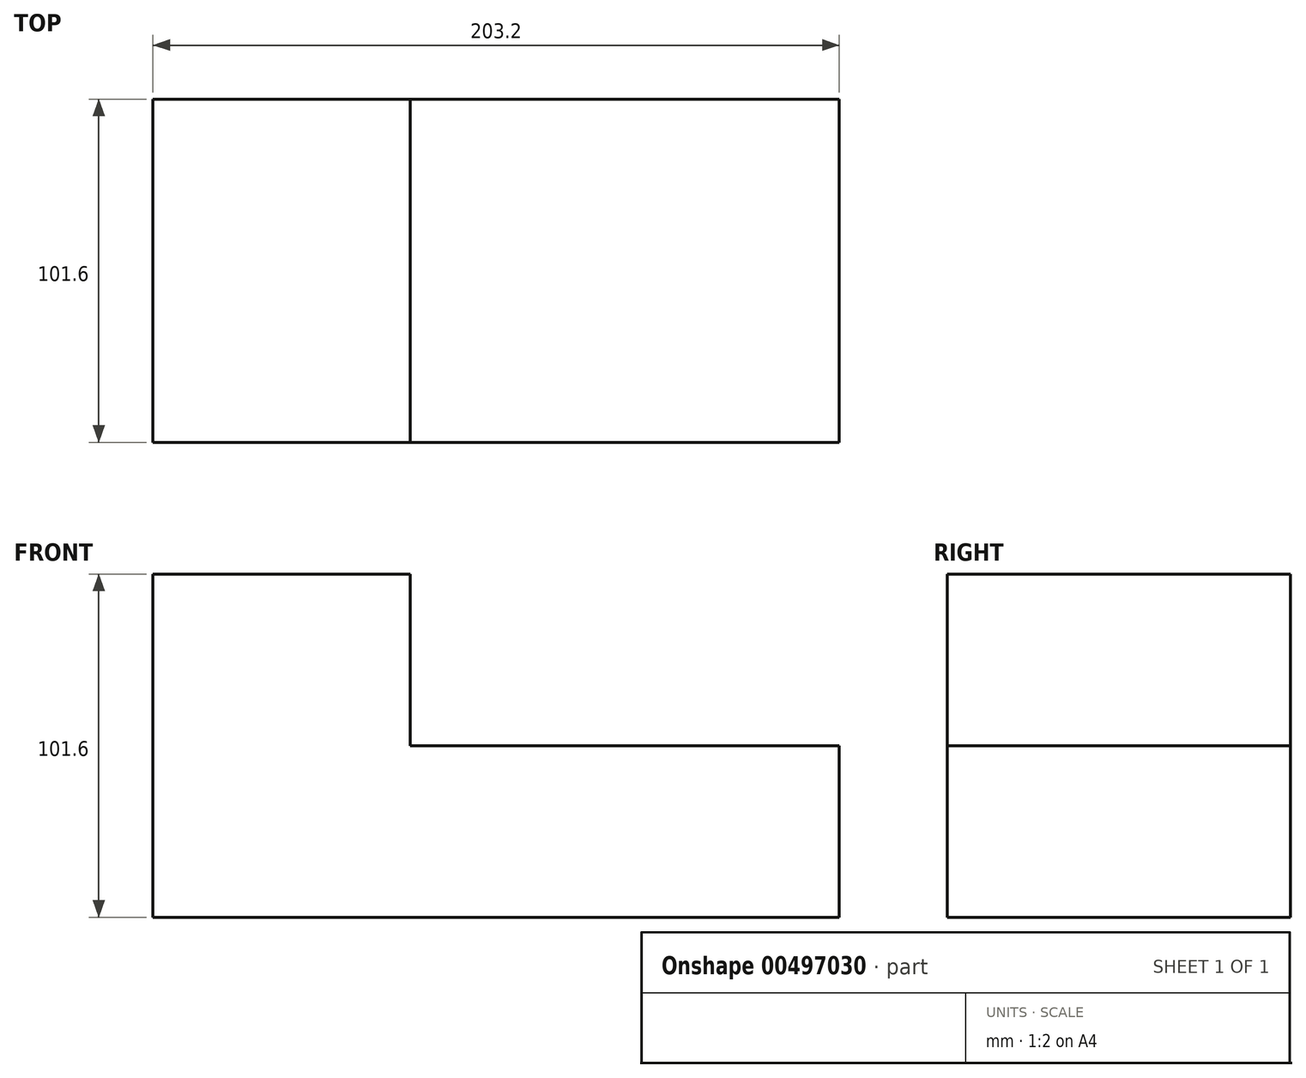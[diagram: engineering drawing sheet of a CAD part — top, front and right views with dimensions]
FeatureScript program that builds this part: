
annotation { "Feature Type Name" : "Feature", "Feature Type Description" : "" }
export const myFeature = defineFeature(function(context is Context, id is Id, definition is map)
    precondition{}
    {
        {
            var Q0;
            Q0=qCreatedBy(makeId("Front.planeOp"),FACE);
            var sketch = newSketch(context, id + "F0", { "sketchPlane" : qUnion([Q0])});
            skLineSegment(sketch, "E0.bottom", {"start": v(0, 0) * mm, "end": v(203.2, 0) * mm});
            skLineSegment(sketch, "E0.top", {"start": v(0, 101.6) * mm, "end": v(203.2, 101.6) * mm});
            skLineSegment(sketch, "E0.left", {"start": v(0, 0) * mm, "end": v(0, 101.6) * mm});
            skLineSegment(sketch, "E0.right", {"start": v(203.2, 0) * mm, "end": v(203.2, 101.6) * mm});
            skLineSegment(sketch, "E1.bottom", {"start": v(203.2, 50.8) * mm, "end": v(76.2, 50.8) * mm});
            skLineSegment(sketch, "E1.top", {"start": v(203.2, 101.6) * mm, "end": v(76.2, 101.6) * mm});
            skLineSegment(sketch, "E1.left", {"start": v(203.2, 50.8) * mm, "end": v(203.2, 101.6) * mm});
            skLineSegment(sketch, "E1.right", {"start": v(76.2, 50.8) * mm, "end": v(76.2, 101.6) * mm});
            skSolve(sketch);
        }
        {
            var Q0;
            Q0=makeQuery(id+"F0.imprint","IMPRINT",FACE,{"disambiguationData":[TD([[makeQuery(id+"F0.imprint","IMPRINT",EDGE,{"derivedFrom":sQuery(id+"F0.wireOp",EDGE,"E0.bottom")}),1.0]])]});
            extrude(context, id + "F1", {"entities" : qUnion([Q0]), "depth" : 101.6 * mm});
        }
    });
